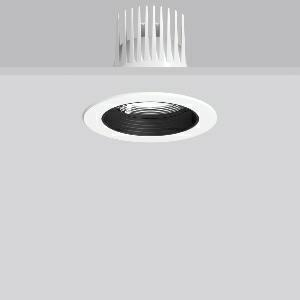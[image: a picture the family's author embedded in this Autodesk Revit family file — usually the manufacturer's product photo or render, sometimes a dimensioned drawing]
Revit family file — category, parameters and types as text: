
# Revit family: heledon_maxi_e_901769_002_3_c64a
name_source: partatom
category: Lighting Fixtures
units: mm (PartAtom-declared; Revit-internal decimal feet)

## family parameters
Cut with Voids When Loaded = No
Host = Face
Light Source = No
Part Type = Normal
Room Calculation Point = No
Round Connector Dimension = Use Diameter
Shared = No

## types (1)
- HELEDON maxi E (1 x LED Modul 935, 3650 lm, 3500)
    Apparent Load = 35 VA
    Approval mark = CE
    CIE Flux Codes = 96 100 100 100 100
    Color Rendering = 92
    Color Temperature = 3500
    Default Elevation = 1800 mm
    Description = Series: HELEDON maxi
Round recessed downlight. Housing: die-cast aluminium, powder-coated. Black plastic ring and recessed LED to prevent glare from the side. Optical assembly with lens made of plastic (polycarbonate) for the best homogeneous light distribution - can be changed without tools. Best colour rendering index Ra>90. Suitable for Recessed ceiling mounting. Installation without tools thanks to spring fastening system. Including separate LED converter with connecting cable 600 mm.High quality converter without flickering and stroboscopic effect. Through-wiring box (5 pole) available as accessory. The following accessories can be mounted without use of tools: interchangeable lenses, decorative glasses, honeycomb louvre, clear and frosted diffusers, white interchangeable plastic ring. 
Colour: traffic white, matt (RAL 9016)
Diameter: 162 mm
Height: 3 mm
Cut-out diameter: 152 mm
Recess height: 200 mm
Luminaire: recess height: 135 mm
Lamp: LED
Socket: without socket
Colour temperature: 3500K
Colour rendering index (CRI): 92
System power: 35 W
Rated luminous flux: 3650 lm
Luminous efficiency: 104 lm/W
Control gear: Regulated power supply
Protection class: II
Type of protection: IP 20
    Height = 0 mm  [stored 0 ft]
    Lamp = 1 x LED Modul 935
    Lamp Light Flux = 3650 lm
    Lamp count = 1
    Length = 162 mm
    Lifetime = 50000 h
    Luminous efficacy = 104 lm/W
    Manufacturer = RZB
    ModVariant = No
    Model = 901769.002.3
    Mounting Place = Ceiling
    Mounting Type = Recessed
    Number of Poles = 1
    OnlyDefault = Yes
    Power Factor = 1
    Product Name = HELEDON maxi E
    Product group = Recessed downlights
    ProductGroupID = 402
    Protection Class = Protection class II
    Protection Degree = IP 20
    RLX_Detail_Level = 1
    RLX_Emergency_Light_Flux = 0 lm
    RLX_Emergency_Type = 0
    RLX_Emergency_Type_DB = No
    RlxData = <blob elided: 118853 chars, md5=fe90213e>
    Socket = socket
    Standby Power = 0 W
    System Light Flux = 3650 lm
    System Power = 35 W
    Type Comments = Product without accessories
    Type Image = 901663.002.jpg
    URL = http://relux.com
    VarID = ---
    Voltage = 230 V
    Voltage Range = 220-240 V
    Weight = 0.00 kg
    Width = 0 mm  [stored 0 ft]

note: [stored X ft] marks values corroborated as IEEE doubles in the binary element streams (Revit-internal decimal feet)

## geometry (parser evidence)
native form markers: Blend x4, Sweep x10
no freeform markers — native parametric forms only
